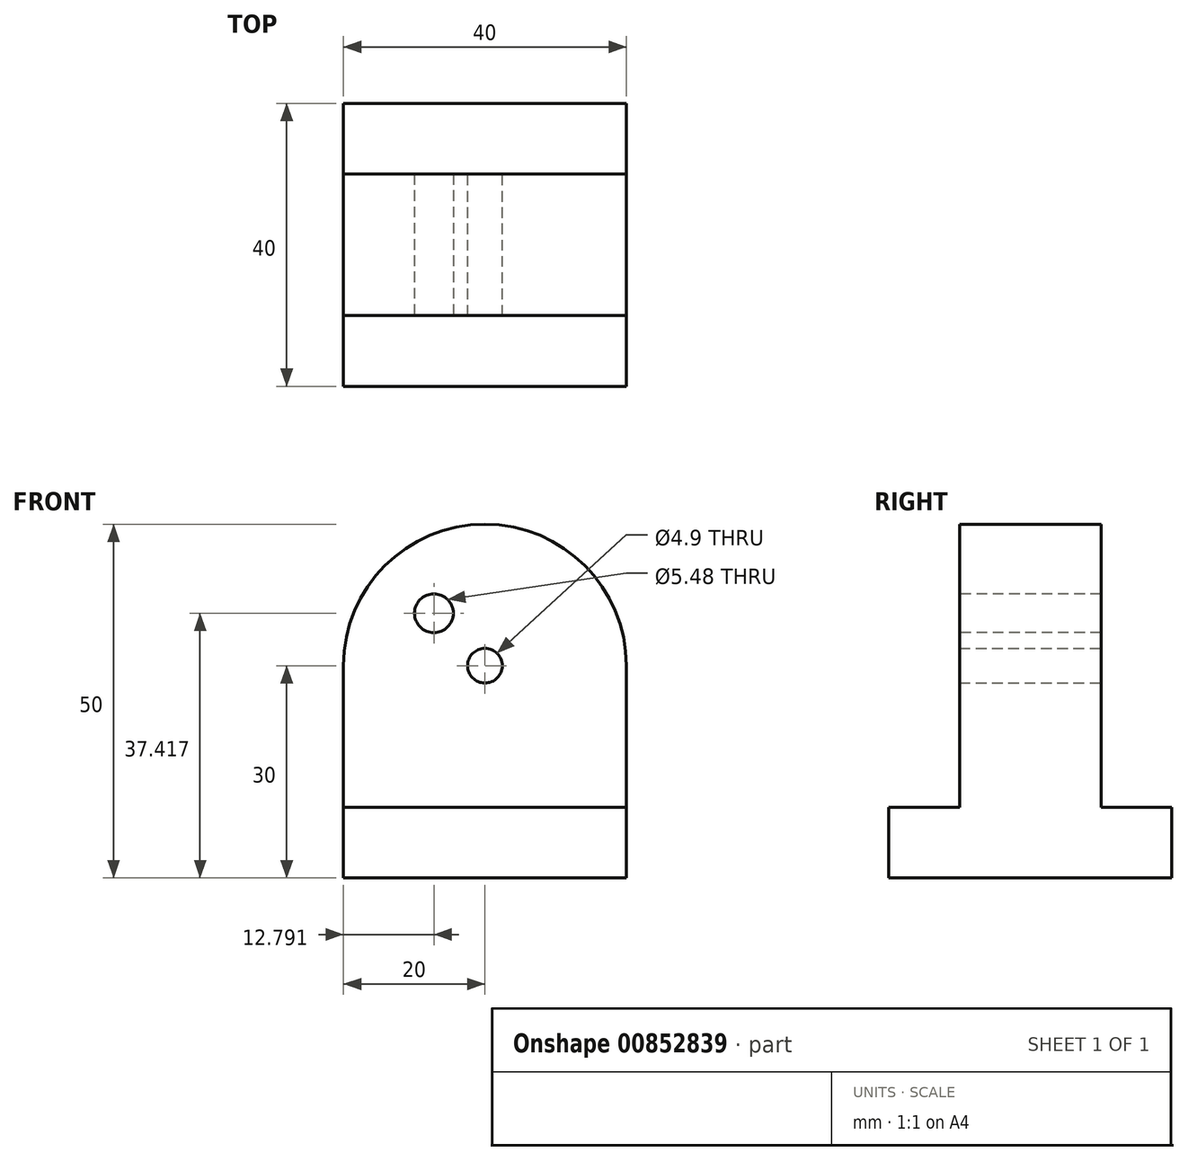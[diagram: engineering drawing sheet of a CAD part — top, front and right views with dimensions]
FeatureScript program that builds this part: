
annotation { "Feature Type Name" : "Feature", "Feature Type Description" : "" }
export const myFeature = defineFeature(function(context is Context, id is Id, definition is map)
    precondition{}
    {
        {
            var Q0;
            Q0=qCreatedBy(makeId("Front.planeOp"),FACE);
            var sketch = newSketch(context, id + "F0", { "sketchPlane" : qUnion([Q0])});
            skLineSegment(sketch, "E0.bottom", {"start": v(20, -20) * mm, "end": v(-20, -20) * mm});
            skLineSegment(sketch, "E0.top", {"start": v(20, 20) * mm, "end": v(-20, 20) * mm});
            skLineSegment(sketch, "E0.left", {"start": v(20, -20) * mm, "end": v(20, 20) * mm});
            skLineSegment(sketch, "E0.right", {"start": v(-20, -20) * mm, "end": v(-20, 20) * mm});
            skPoint(sketch, "E0.middle", {"position": v(0, 0) * mm});
            skCircle(sketch, "E1", {"center": v(0, 0) * mm, "radius": 2.45 * mm});
            skLineSegment(sketch, "E2", {"start": v(-20, 20) * mm, "end": v(0, 0) * mm});
            skLineSegment(sketch, "E3", {"start": v(0, 0) * mm, "end": v(20, 20) * mm});
            skCircle(sketch, "E4", {"center": v(0, 0) * mm, "radius": 20 * mm});
            skSolve(sketch);
        }
        {
            var Q0;
            {var subQ4=sQuery(id+"F0.wireOp",EDGE,"E1");var subQ6=sQuery(id+"F0.wireOp",EDGE,"E2");var subQ7=makeQuery(id+"F0.imprint","INTERSECT",VERTEX,{"derivedFrom":[subQ4,subQ6]});Q0=makeQuery(id+"F0.imprint","IMPRINT",FACE,{"disambiguationData":[TD([[makeQuery(id+"F0.imprint","IMPRINT",EDGE,{"disambiguationData":[TD([[subQ7,1.0]])],"derivedFrom":subQ4}),-1.0]])]});}
            var Q1;
            {var subQ4=sQuery(id+"F0.wireOp",EDGE,"E2");var subQ5=sQuery(id+"F0.wireOp",EDGE,"E1");var subQ6=makeQuery(id+"F0.imprint","INTERSECT",VERTEX,{"derivedFrom":[subQ5,subQ4]});Q1=makeQuery(id+"F0.imprint","IMPRINT",FACE,{"disambiguationData":[TD([[makeQuery(id+"F0.imprint","IMPRINT",EDGE,{"disambiguationData":[TD([[subQ6,-1.0]])],"derivedFrom":subQ5}),-1.0]])]});}
            var Q2;
            {var subQ0=sQuery(id+"F0.wireOp",EDGE,"E0.right");var subQ1=sQuery(id+"F0.wireOp",EDGE,"E0.bottom");var subQ2=makeQuery(id+"F0.imprint","INTERSECT",VERTEX,{"derivedFrom":[subQ1,subQ0]});Q2=makeQuery(id+"F0.imprint","IMPRINT",FACE,{"disambiguationData":[TD([[makeQuery(id+"F0.imprint","IMPRINT",EDGE,{"disambiguationData":[TD([[subQ2,1.0]])],"derivedFrom":subQ1}),-1.0]])]});}
            var Q3;
            {var subQ0=sQuery(id+"F0.wireOp",EDGE,"E0.left");var subQ1=sQuery(id+"F0.wireOp",EDGE,"E0.bottom");var subQ2=makeQuery(id+"F0.imprint","INTERSECT",VERTEX,{"derivedFrom":[subQ1,subQ0]});Q3=makeQuery(id+"F0.imprint","IMPRINT",FACE,{"disambiguationData":[TD([[makeQuery(id+"F0.imprint","IMPRINT",EDGE,{"disambiguationData":[TD([[subQ2,-1.0]])],"derivedFrom":subQ1}),-1.0]])]});}
            extrude(context, id + "F1", {"entities" : qUnion([Q0, Q1, Q2, Q3]), "endBound" : BoundingType.SYMMETRIC, "depth" : 20 * mm, "offsetDistance" : 25 * mm});
        }
        {
            var Q0;
            Q0=makeQuery(id+"F1.opExtrude","CAP_FACE",FACE,{"disambiguationData":[OSD([sQuery(id+"F0.wireOp",EDGE,"E0.bottom"),sQuery(id+"F0.wireOp",EDGE,"E0.left"),sQuery(id+"F0.wireOp",EDGE,"E0.right"),sQuery(id+"F0.wireOp",EDGE,"E1"),sQuery(id+"F0.wireOp",EDGE,"E4")])],"isStart":false});
            var sketch = newSketch(context, id + "F2", { "sketchPlane" : qUnion([Q0])});
            skCircle(sketch, "E5", {"center": v(-7.2, 7.42) * mm, "radius": 2.74 * mm});
            skSolve(sketch);
        }
        {
            var Q0;
            Q0=makeQuery(id+"F2.imprint","IMPRINT",FACE,{"disambiguationData":[TD([[makeQuery(id+"F2.imprint","IMPRINT",EDGE,{"derivedFrom":sQuery(id+"F2.wireOp",EDGE,"E5")}),1.0]])]});
            extrude(context, id + "F3", {"entities" : qUnion([Q0]), "operationType" : NewBodyOperationType.REMOVE, "oppositeDirection" : true, "depth" : 25 * mm, "offsetDistance" : 25 * mm});
        }
        {
            var Q0;
            Q0=makeQuery(id+"F1.opExtrude","SWEPT_FACE",FACE,{"disambiguationData":[OSD([sQuery(id+"F0.wireOp",EDGE,"E0.bottom")])]});
            var sketch = newSketch(context, id + "F4", { "sketchPlane" : qUnion([Q0])});
            skLineSegment(sketch, "E6.bottom", {"start": v(-20, -20) * mm, "end": v(20, -20) * mm});
            skLineSegment(sketch, "E6.top", {"start": v(-20, 20) * mm, "end": v(20, 20) * mm});
            skLineSegment(sketch, "E6.left", {"start": v(-20, -20) * mm, "end": v(-20, 20) * mm});
            skLineSegment(sketch, "E6.right", {"start": v(20, -20) * mm, "end": v(20, 20) * mm});
            skPoint(sketch, "E6.middle", {"position": v(0, 0) * mm});
            skSolve(sketch);
        }
        {
            var Q0;
            {var subQ0=sQuery(id+"F4.wireOp",EDGE,"E6.top");Q0=makeQuery(id+"F4.imprint","IMPRINT",FACE,{"disambiguationData":[TD([[makeQuery(id+"F4.imprint","IMPRINT",EDGE,{"derivedFrom":subQ0}),-1.0]])]});}
            var Q1;
            {var subQ1=sQuery(id+"F0.wireOp",EDGE,"E0.bottom");var subQ2=makeQuery(id+"F1.opExtrude","CAP_EDGE",EDGE,{"disambiguationData":[OSD([subQ1])],"isStart":true});Q1=makeQuery(id+"F4.imprint","IMPRINT",FACE,{"disambiguationData":[TD([[makeQuery(id+"F4.imprint","IMPRINT",EDGE,{"derivedFrom":subQ2}),-1.0]])]});}
            var Q2;
            {var subQ0=sQuery(id+"F4.wireOp",EDGE,"E6.bottom");Q2=makeQuery(id+"F4.imprint","IMPRINT",FACE,{"disambiguationData":[TD([[makeQuery(id+"F4.imprint","IMPRINT",EDGE,{"derivedFrom":subQ0}),1.0]])]});}
            extrude(context, id + "F5", {"entities" : qUnion([Q0, Q1, Q2]), "operationType" : NewBodyOperationType.ADD, "depth" : 10 * mm, "offsetDistance" : 25 * mm});
        }
    });
